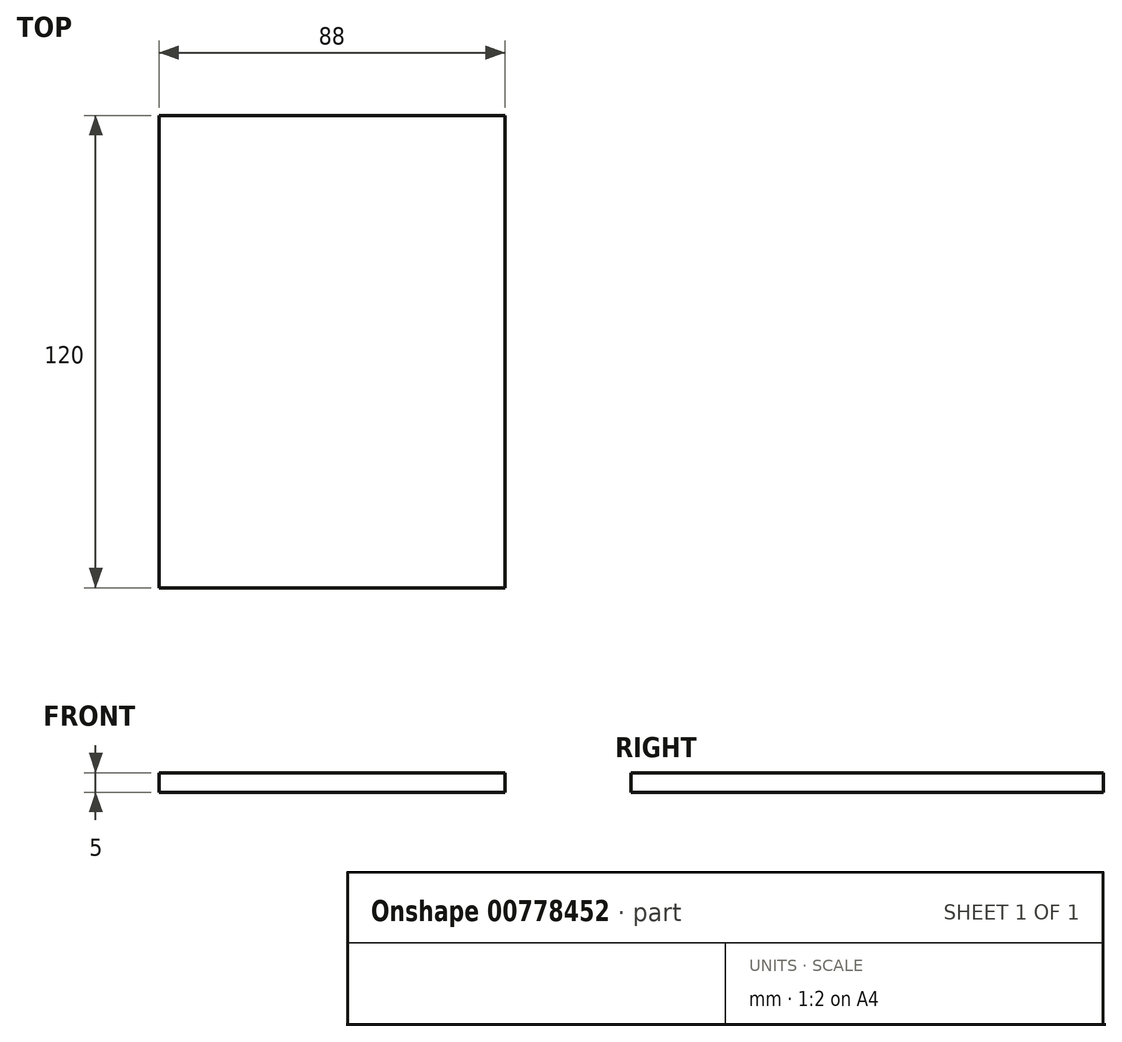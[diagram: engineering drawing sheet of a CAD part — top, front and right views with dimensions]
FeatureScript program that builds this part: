
annotation { "Feature Type Name" : "Feature", "Feature Type Description" : "" }
export const myFeature = defineFeature(function(context is Context, id is Id, definition is map)
    precondition{}
    {
        {
            var Q0;
            Q0=qCreatedBy(makeId("Top.planeOp"),FACE);
            var sketch = newSketch(context, id + "F0", { "sketchPlane" : qUnion([Q0])});
            skLineSegment(sketch, "E0.bottom", {"start": v(44, 60) * mm, "end": v(-44, 60) * mm});
            skLineSegment(sketch, "E0.top", {"start": v(44, -60) * mm, "end": v(-44, -60) * mm});
            skLineSegment(sketch, "E0.left", {"start": v(44, 60) * mm, "end": v(44, -60) * mm});
            skLineSegment(sketch, "E0.right", {"start": v(-44, 60) * mm, "end": v(-44, -60) * mm});
            skPoint(sketch, "E0.middle", {"position": v(0, 0) * mm});
            skSolve(sketch);
        }
        {
            var Q0;
            Q0 = qSketchRegion(id + "F0", true);
            extrude(context, id + "F1", {"entities" : qUnion([Q0]), "depth" : 5 * mm, "offsetDistance" : 25 * mm});
        }
        {
            var Q0;
            Q0=makeQuery(id+"F1.opExtrude","SWEPT_FACE",FACE,{"disambiguationData":[OSD([sQuery(id+"F0.wireOp",EDGE,"E0.top")])]});
            var sketch = newSketch(context, id + "F2", { "sketchPlane" : qUnion([Q0])});
            skLineSegment(sketch, "E1", {"start": v(-41.27, 5) * mm, "end": v(-43, 2) * mm});
            skLineSegment(sketch, "E2", {"start": v(-43, 2) * mm, "end": v(43, 2) * mm});
            skLineSegment(sketch, "E3", {"start": v(43, 2) * mm, "end": v(41.27, 5) * mm});
            skLineSegment(sketch, "E4", {"start": v(41.27, 5) * mm, "end": v(-41.27, 5) * mm});
            skSolve(sketch);
        }
        {
            var Q0;
            Q0 = qSketchRegion(id + "F2", true);
            extrude(context, id + "F3", {"entities" : qUnion([Q0]), "operationType" : NewBodyOperationType.REMOVE, "oppositeDirection" : true, "depth" : 117 * mm, "offsetDistance" : 25 * mm});
        }
        {
            var Q0;
            Q0=makeQuery(id+"F3.boolean.opBoolean","COPY",FACE,{"derivedFrom":makeQuery(id+"F3.opExtrude","CAP_FACE",FACE,{"disambiguationData":[OSD([sQuery(id+"F2.wireOp",EDGE,"E1"),sQuery(id+"F2.wireOp",EDGE,"E2"),sQuery(id+"F2.wireOp",EDGE,"E3"),sQuery(id+"F2.wireOp",EDGE,"E4")])],"isStart":false})});
            var sketch = newSketch(context, id + "F4", { "sketchPlane" : qUnion([Q0])});
            skSolve(sketch);
        }
        {
            var Q0;
            Q0 = qSketchRegion(id + "F4", true);
            var Q1;
            Q1=makeQuery(id+"F4.imprint","IMPRINT",FACE,{"disambiguationData":[TD([[makeQuery(id+"F4.imprint","IMPRINT",EDGE,{"derivedFrom":makeQuery(id+"F3.boolean.opBoolean","COPY",EDGE,{"derivedFrom":makeQuery(id+"F3.opExtrude","CAP_EDGE",EDGE,{"disambiguationData":[OSD([sQuery(id+"F2.wireOp",EDGE,"E1")])],"isStart":false})})}),1.0]])]});
            extrude(context, id + "F5", {"entities" : qUnion([Q0, Q1]), "operationType" : NewBodyOperationType.ADD, "depth" : 117 * mm, "offsetDistance" : 25 * mm});
        }
    });
